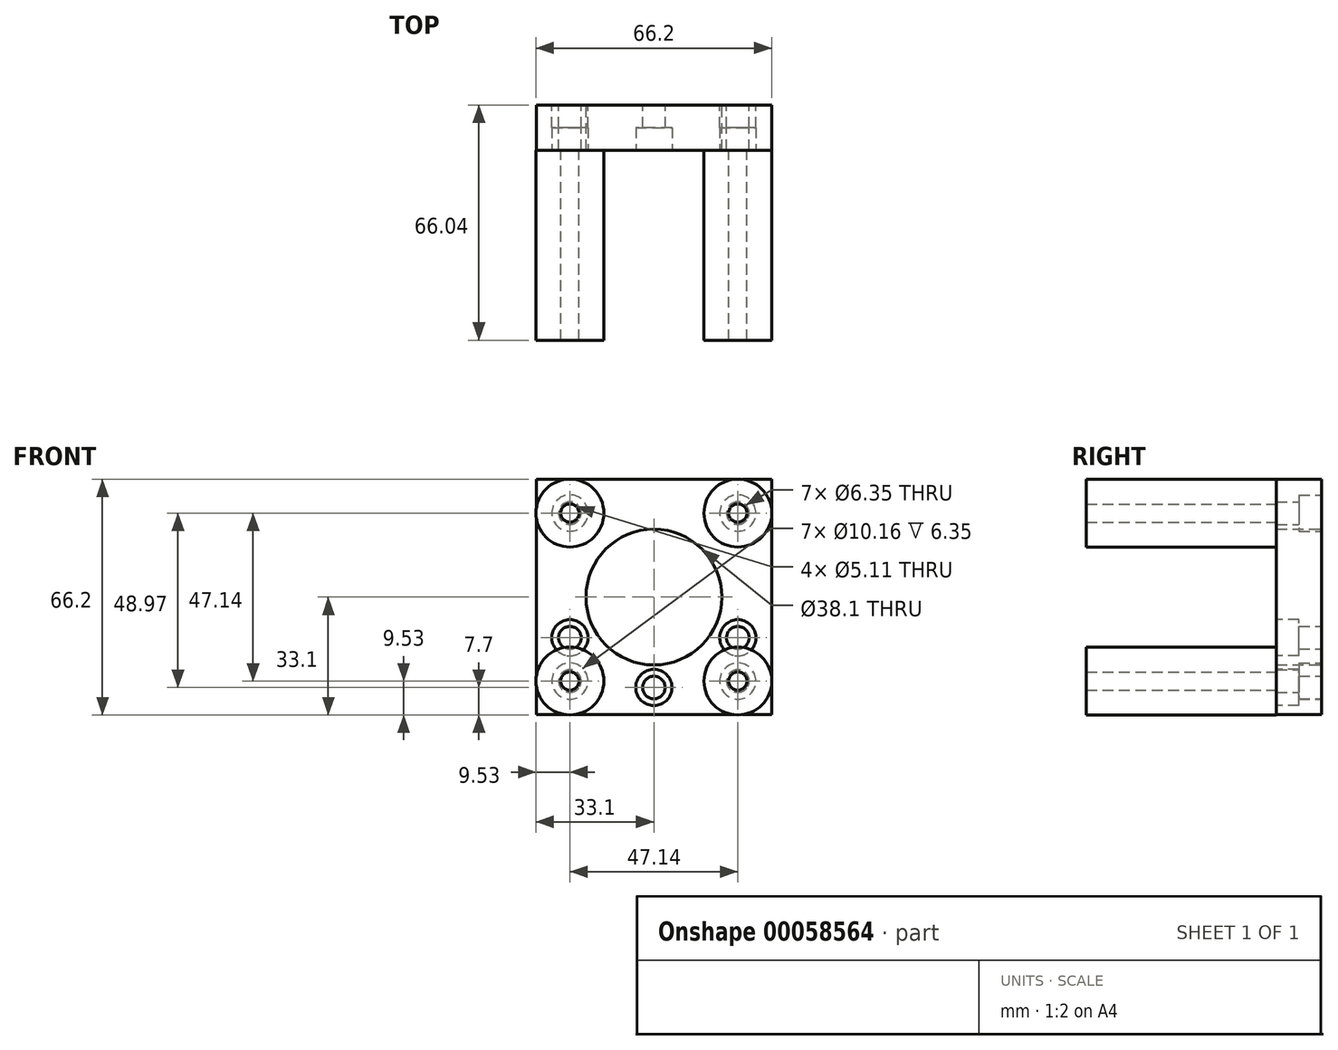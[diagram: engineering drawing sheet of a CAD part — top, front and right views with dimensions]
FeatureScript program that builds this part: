
annotation { "Feature Type Name" : "Feature", "Feature Type Description" : "" }
export const myFeature = defineFeature(function(context is Context, id is Id, definition is map)
    precondition{}
    {
        {
            var Q0;
            Q0=qCreatedBy(makeId("Front.planeOp"),FACE);
            var sketch = newSketch(context, id + "F0", { "sketchPlane" : qUnion([Q0])});
            skLineSegment(sketch, "E0.rect.bottom", {"start": v(33.02, 33.02) * mm, "end": v(-33.02, 33.02) * mm});
            skLineSegment(sketch, "E0.rect.top", {"start": v(33.02, -33.02) * mm, "end": v(-33.02, -33.02) * mm});
            skLineSegment(sketch, "E0.rect.left", {"start": v(33.02, 33.02) * mm, "end": v(33.02, -33.02) * mm});
            skLineSegment(sketch, "E0.rect.right", {"start": v(-33.02, 33.02) * mm, "end": v(-33.02, -33.02) * mm});
            skPoint(sketch, "E0.rect.middle", {"position": v(0, 0) * mm});
            skLineSegment(sketch, "E1.rect.bottom", {"start": v(23.57, 23.57) * mm, "end": v(-23.57, 23.57) * mm, "construction": true});
            skLineSegment(sketch, "E1.rect.top", {"start": v(23.57, -23.57) * mm, "end": v(-23.57, -23.57) * mm, "construction": true});
            skLineSegment(sketch, "E1.rect.left", {"start": v(23.57, 23.57) * mm, "end": v(23.57, -23.57) * mm, "construction": true});
            skLineSegment(sketch, "E1.rect.right", {"start": v(-23.57, 23.57) * mm, "end": v(-23.57, -23.57) * mm, "construction": true});
            skCircle(sketch, "E2", {"center": v(-23.57, 23.57) * mm, "radius": 3.18 * mm});
            skCircle(sketch, "E3", {"center": v(-23.57, -23.57) * mm, "radius": 3.18 * mm});
            skCircle(sketch, "E4", {"center": v(23.57, -23.57) * mm, "radius": 3.18 * mm});
            skCircle(sketch, "E5", {"center": v(23.57, 23.57) * mm, "radius": 3.18 * mm});
            skCircle(sketch, "E6", {"center": v(0, 0) * mm, "radius": 19.05 * mm});
            skCircle(sketch, "E7", {"center": v(0, 0) * mm, "radius": 17.02 * mm, "construction": true});
            skPoint(sketch, "E8", {"position": v(0, -17.02) * mm});
            skSolve(sketch);
        }
        {
            var Q0;
            Q0 = qSketchRegion(id + "F0", true);
            extrude(context, id + "F1", {"entities" : qUnion([Q0]), "depth" : 12.7 * mm});
        }
        {
            var Q0;
            Q0=makeQuery(id+"F1.opExtrude","CAP_FACE",FACE,{"disambiguationData":[OSD([sQuery(id+"F0.wireOp",EDGE,"E0.rect.bottom"),sQuery(id+"F0.wireOp",EDGE,"E0.rect.top"),sQuery(id+"F0.wireOp",EDGE,"E0.rect.left"),sQuery(id+"F0.wireOp",EDGE,"E0.rect.right"),sQuery(id+"F0.wireOp",EDGE,"E2"),sQuery(id+"F0.wireOp",EDGE,"E3"),sQuery(id+"F0.wireOp",EDGE,"E4"),sQuery(id+"F0.wireOp",EDGE,"E5")])],"isStart":true});
            var sketch = newSketch(context, id + "F2", { "sketchPlane" : qUnion([Q0])});
            skCircle(sketch, "E9", {"center": v(23.57, -23.57) * mm, "radius": 5.08 * mm});
            skCircle(sketch, "E10", {"center": v(-23.57, -23.57) * mm, "radius": 5.08 * mm});
            skCircle(sketch, "E11", {"center": v(-23.57, 23.57) * mm, "radius": 5.08 * mm});
            skCircle(sketch, "E12", {"center": v(23.57, 23.57) * mm, "radius": 5.08 * mm});
            skSolve(sketch);
        }
        {
            var Q0;
            Q0 = qSketchRegion(id + "F2", true);
            extrude(context, id + "F3", {"entities" : qUnion([Q0]), "operationType" : NewBodyOperationType.REMOVE, "oppositeDirection" : true, "depth" : 6.35 * mm});
        }
        {
            var Q0;
            Q0=makeQuery(id+"F1.opExtrude","CAP_FACE",FACE,{"disambiguationData":[OSD([sQuery(id+"F0.wireOp",EDGE,"E0.rect.bottom"),sQuery(id+"F0.wireOp",EDGE,"E0.rect.top"),sQuery(id+"F0.wireOp",EDGE,"E0.rect.left"),sQuery(id+"F0.wireOp",EDGE,"E0.rect.right"),sQuery(id+"F0.wireOp",EDGE,"E2"),sQuery(id+"F0.wireOp",EDGE,"E3"),sQuery(id+"F0.wireOp",EDGE,"E4"),sQuery(id+"F0.wireOp",EDGE,"E5"),sQuery(id+"F0.wireOp",EDGE,"E6")])],"isStart":true});
            var sketch = newSketch(context, id + "F4", { "sketchPlane" : qUnion([Q0])});
            skLineSegment(sketch, "E13", {"start": v(33.02, -11.43) * mm, "end": v(-33.02, -11.43) * mm, "construction": true});
            skPoint(sketch, "E13.endSnap0", {"position": v(-33.02, 0) * mm});
            skLineSegment(sketch, "E14.rect.top", {"start": v(23.57, 23.57) * mm, "end": v(-23.57, 23.57) * mm, "construction": true});
            skLineSegment(sketch, "E14.rect.left", {"start": v(23.57, -23.57) * mm, "end": v(23.57, 23.57) * mm, "construction": true});
            skLineSegment(sketch, "E14.rect.right", {"start": v(-23.57, -23.57) * mm, "end": v(-23.57, 23.57) * mm, "construction": true});
            skPoint(sketch, "E14.rect.middle", {"position": v(0, 0) * mm});
            skCircle(sketch, "E15", {"center": v(23.57, -11.43) * mm, "radius": 3.18 * mm});
            skCircle(sketch, "E16", {"center": v(-23.57, -11.43) * mm, "radius": 3.18 * mm});
            skCircle(sketch, "E17", {"center": v(23.57, -11.43) * mm, "radius": 5.08 * mm, "construction": true});
            skCircle(sketch, "E18", {"center": v(0, -25.4) * mm, "radius": 3.18 * mm});
            skSolve(sketch);
        }
        {
            var Q0;
            Q0 = qSketchRegion(id + "F4", true);
            extrude(context, id + "F5", {"entities" : qUnion([Q0]), "operationType" : NewBodyOperationType.REMOVE, "endBound" : BoundingType.THROUGH_ALL, "oppositeDirection" : true, "depth" : 25.4 * mm});
        }
        {
            var Q0;
            Q0=makeQuery(id+"F1.opExtrude","CAP_FACE",FACE,{"disambiguationData":[OSD([sQuery(id+"F0.wireOp",EDGE,"E0.rect.bottom"),sQuery(id+"F0.wireOp",EDGE,"E0.rect.top"),sQuery(id+"F0.wireOp",EDGE,"E0.rect.left"),sQuery(id+"F0.wireOp",EDGE,"E0.rect.right"),sQuery(id+"F0.wireOp",EDGE,"E2"),sQuery(id+"F0.wireOp",EDGE,"E3"),sQuery(id+"F0.wireOp",EDGE,"E4"),sQuery(id+"F0.wireOp",EDGE,"E5"),sQuery(id+"F0.wireOp",EDGE,"E6")])],"isStart":false});
            var sketch = newSketch(context, id + "F6", { "sketchPlane" : qUnion([Q0])});
            skCircle(sketch, "E19", {"center": v(23.57, -11.43) * mm, "radius": 5.08 * mm});
            skCircle(sketch, "E20", {"center": v(0, -25.4) * mm, "radius": 5.08 * mm});
            skCircle(sketch, "E21", {"center": v(-23.57, -11.43) * mm, "radius": 5.08 * mm});
            skSolve(sketch);
        }
        {
            var Q0;
            Q0 = qSketchRegion(id + "F6", true);
            extrude(context, id + "F7", {"entities" : qUnion([Q0]), "operationType" : NewBodyOperationType.REMOVE, "oppositeDirection" : true, "depth" : 6.35 * mm});
        }
        {
            var Q0;
            Q0=makeQuery(id+"F1.opExtrude","CAP_FACE",FACE,{"disambiguationData":[OSD([sQuery(id+"F0.wireOp",EDGE,"E0.rect.bottom"),sQuery(id+"F0.wireOp",EDGE,"E0.rect.top"),sQuery(id+"F0.wireOp",EDGE,"E0.rect.left"),sQuery(id+"F0.wireOp",EDGE,"E0.rect.right"),sQuery(id+"F0.wireOp",EDGE,"E2"),sQuery(id+"F0.wireOp",EDGE,"E3"),sQuery(id+"F0.wireOp",EDGE,"E4"),sQuery(id+"F0.wireOp",EDGE,"E5"),sQuery(id+"F0.wireOp",EDGE,"E6")])],"isStart":false});
            var sketch = newSketch(context, id + "F8", { "sketchPlane" : qUnion([Q0])});
            skCircle(sketch, "E22", {"center": v(23.57, -23.57) * mm, "radius": 9.53 * mm});
            skCircle(sketch, "E23", {"center": v(-23.57, -23.57) * mm, "radius": 7.06 * mm, "construction": true});
            skCircle(sketch, "E24", {"center": v(-23.57, -23.57) * mm, "radius": 9.53 * mm});
            skCircle(sketch, "E25", {"center": v(23.57, 23.57) * mm, "radius": 9.53 * mm});
            skCircle(sketch, "E26", {"center": v(-23.57, 23.57) * mm, "radius": 9.53 * mm});
            skCircle(sketch, "E27", {"center": v(23.57, -23.57) * mm, "radius": 2.55 * mm});
            skCircle(sketch, "E28", {"center": v(-23.57, -23.57) * mm, "radius": 2.55 * mm});
            skCircle(sketch, "E29", {"center": v(23.57, 23.57) * mm, "radius": 2.55 * mm});
            skCircle(sketch, "E30", {"center": v(-23.57, 23.57) * mm, "radius": 2.55 * mm});
            skSolve(sketch);
        }
        {
            var Q0;
            Q0 = qSketchRegion(id + "F8", true);
            extrude(context, id + "F9", {"entities" : qUnion([Q0]), "depth" : 53.34 * mm});
        }
    });
